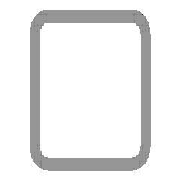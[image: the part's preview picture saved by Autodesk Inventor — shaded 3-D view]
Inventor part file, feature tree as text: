
AUTODESK INVENTOR PART (.ipt)
format: ipt  version: 2021 (Build 250183000, 183)  size: 144,896 bytes
history: native  units: mm (DEFAULTED — no unit token found)
features: other x5, sketch x3, extrude x1, split x1, plane x1
ambient origin geometry x8: Origin, YZ Plane, XZ Plane, XY Plane, X Axis, Y Axis, Z Axis, Center Point
bodies: Solid1 (feature_tree)
feature tree (11):
  parser-record x1  (decoder bookkeeping rows leaked as tree rows — omitted from the tree; the rows remain in map.json)
  other  "Driven Length"
  other  "Plano inicial"
  other  "Plano final"
  extrude  "Corpo"  TaperAngle=0.0deg  [1 undecoded]
  other  "Plano de trabalho4"
  split  "Dividir1"
  sketch  "Esboço"  dims[d11=50.8mm d12=4.7625mm d13=-15.698063mm d14=2236.067977mm d15=25.4mm d16=25.4mm d17=9.525mm d18=90.0deg d19=2251.766041mm]
  sketch  "Sketch3"  dims[d3=2251.766041mm d4=0.0mm]
  plane  "Work Plane3"
  sketch  "Sketch4"  dims[d10=50.8mm]
note: 1 required parameter value undecoded (feature->parameter linkage not recoverable at this tier; creation-order binding heuristic only, values carry confidence <= 0.55)
